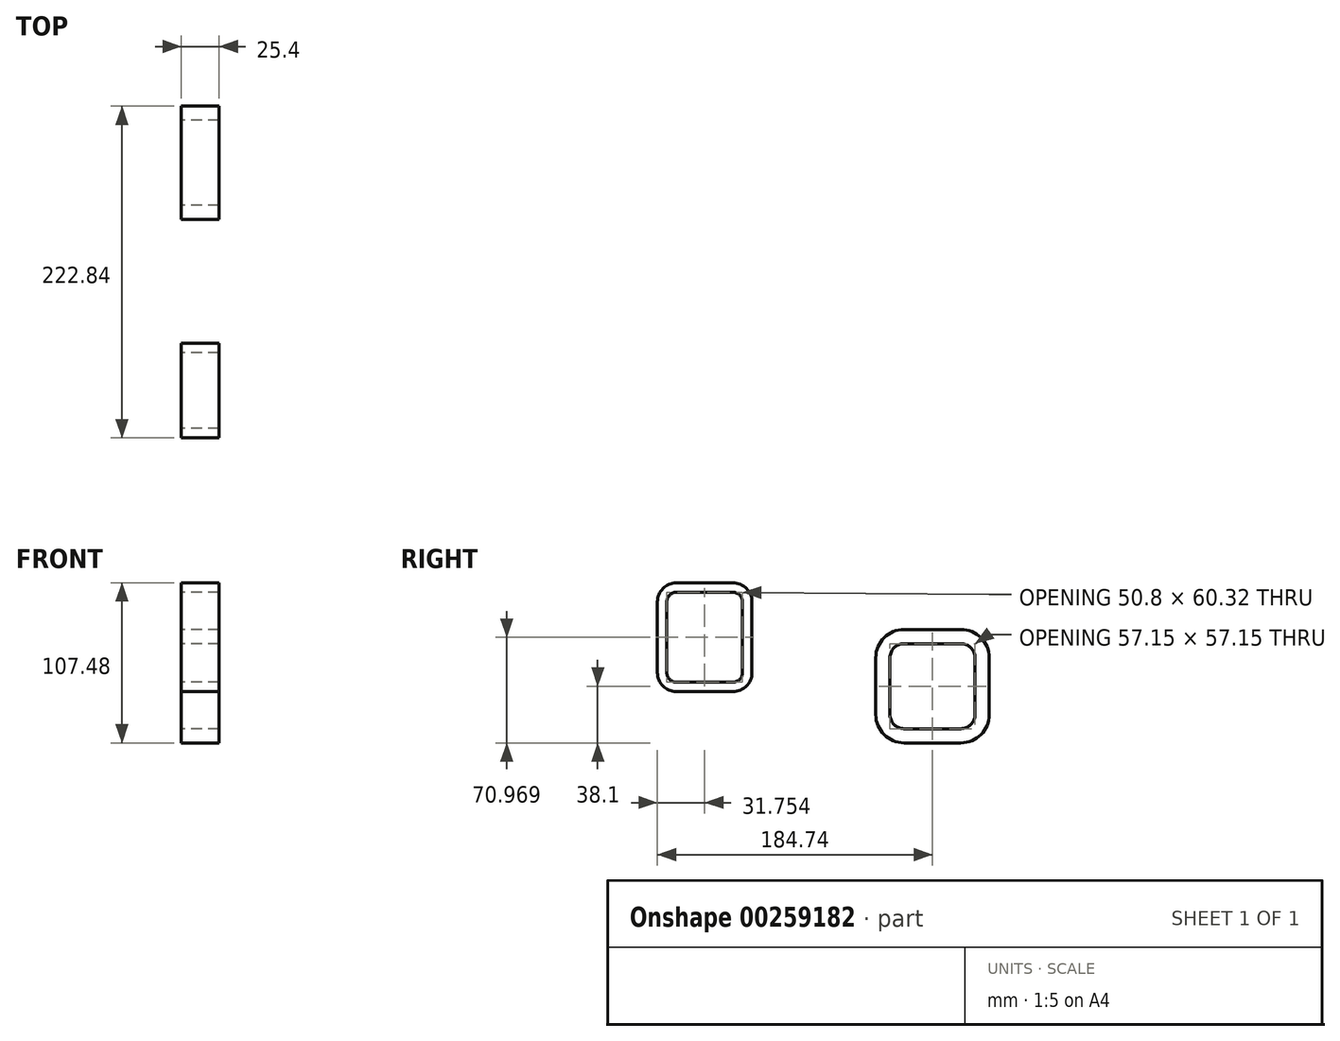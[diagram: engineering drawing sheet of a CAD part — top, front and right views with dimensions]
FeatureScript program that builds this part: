
annotation { "Feature Type Name" : "Feature", "Feature Type Description" : "" }
export const myFeature = defineFeature(function(context is Context, id is Id, definition is map)
    precondition{}
    {
        {
            var Q0;
            Q0=qCreatedBy(makeId("Right.planeOp"),FACE);
            var sketch = newSketch(context, id + "F0", { "sketchPlane" : qUnion([Q0])});
            skLineSegment(sketch, "E0.bottom", {"start": v(-19.05, 38.1) * mm, "end": v(19.05, 38.1) * mm});
            skLineSegment(sketch, "E0.top", {"start": v(-19.05, -38.1) * mm, "end": v(19.05, -38.1) * mm});
            skLineSegment(sketch, "E0.left", {"start": v(-38.1, 19.05) * mm, "end": v(-38.1, -19.05) * mm});
            skLineSegment(sketch, "E0.right", {"start": v(38.1, 19.05) * mm, "end": v(38.1, -19.05) * mm});
            skLineSegment(sketch, "E1.bottom", {"start": v(-19.05, 28.58) * mm, "end": v(19.05, 28.58) * mm});
            skLineSegment(sketch, "E1.top", {"start": v(-19.05, -28.58) * mm, "end": v(19.05, -28.58) * mm});
            skLineSegment(sketch, "E1.left", {"start": v(-28.58, 19.05) * mm, "end": v(-28.58, -19.05) * mm});
            skLineSegment(sketch, "E1.right", {"start": v(28.58, 19.05) * mm, "end": v(28.58, -19.05) * mm});
            skPoint(sketch, "E2.visualSharp", {"position": v(-28.58, 28.58) * mm});
            skArc(sketch, "E2.filletArc", {"start": v(-19.05, 28.58) * mm, "mid": v(-25.79, 25.79) * mm, "end": v(-28.58, 19.05) * mm});
            skPoint(sketch, "E3.visualSharp", {"position": v(-28.58, -28.58) * mm});
            skArc(sketch, "E3.filletArc", {"start": v(-28.58, -19.05) * mm, "mid": v(-25.79, -25.79) * mm, "end": v(-19.05, -28.58) * mm});
            skPoint(sketch, "E4.visualSharp", {"position": v(28.58, -28.58) * mm});
            skArc(sketch, "E4.filletArc", {"start": v(19.05, -28.58) * mm, "mid": v(25.79, -25.79) * mm, "end": v(28.58, -19.05) * mm});
            skPoint(sketch, "E5.visualSharp", {"position": v(28.58, 28.58) * mm});
            skArc(sketch, "E5.filletArc", {"start": v(28.58, 19.05) * mm, "mid": v(25.79, 25.79) * mm, "end": v(19.05, 28.58) * mm});
            skPoint(sketch, "E6.visualSharp", {"position": v(-38.1, 38.1) * mm});
            skArc(sketch, "E6.filletArc", {"start": v(-19.05, 38.1) * mm, "mid": v(-32.52, 32.52) * mm, "end": v(-38.1, 19.05) * mm});
            skPoint(sketch, "E7.visualSharp", {"position": v(-38.1, -38.1) * mm});
            skArc(sketch, "E7.filletArc", {"start": v(-38.1, -19.05) * mm, "mid": v(-32.52, -32.52) * mm, "end": v(-19.05, -38.1) * mm});
            skPoint(sketch, "E8.visualSharp", {"position": v(38.1, -38.1) * mm});
            skArc(sketch, "E8.filletArc", {"start": v(19.05, -38.1) * mm, "mid": v(32.52, -32.52) * mm, "end": v(38.1, -19.05) * mm});
            skPoint(sketch, "E9.visualSharp", {"position": v(38.1, 38.1) * mm});
            skArc(sketch, "E9.filletArc", {"start": v(38.1, 19.05) * mm, "mid": v(32.52, 32.52) * mm, "end": v(19.05, 38.1) * mm});
            skSolve(sketch);
        }
        {
            var Q0;
            Q0=qSketchRegion(id+"F0",true);
            extrude(context, id + "F1", {"entities" : qUnion([Q0]), "depth" : 25.4 * mm});
        }
        {
            var Q0;
            Q0=qCreatedBy(makeId("Right.planeOp"),FACE);
            var sketch = newSketch(context, id + "F2", { "sketchPlane" : qUnion([Q0])});
            skLineSegment(sketch, "E10.bottom", {"start": v(-172.04, 69.38) * mm, "end": v(-133.94, 69.38) * mm});
            skLineSegment(sketch, "E10.top", {"start": v(-172.04, -3.64) * mm, "end": v(-133.94, -3.64) * mm});
            skLineSegment(sketch, "E10.left", {"start": v(-184.74, 56.68) * mm, "end": v(-184.74, 9.06) * mm});
            skLineSegment(sketch, "E10.right", {"start": v(-121.24, 56.68) * mm, "end": v(-121.24, 9.06) * mm});
            skLineSegment(sketch, "E11.bottom", {"start": v(-172.04, 63.03) * mm, "end": v(-133.94, 63.03) * mm});
            skLineSegment(sketch, "E11.top", {"start": v(-172.04, 2.7) * mm, "end": v(-133.94, 2.7) * mm});
            skLineSegment(sketch, "E11.left", {"start": v(-178.39, 56.68) * mm, "end": v(-178.39, 9.06) * mm});
            skLineSegment(sketch, "E11.right", {"start": v(-127.59, 56.68) * mm, "end": v(-127.59, 9.06) * mm});
            skPoint(sketch, "E12.visualSharp", {"position": v(-178.39, 63.03) * mm});
            skArc(sketch, "E12.filletArc", {"start": v(-172.04, 63.03) * mm, "mid": v(-176.53, 61.17) * mm, "end": v(-178.39, 56.68) * mm});
            skPoint(sketch, "E13.visualSharp", {"position": v(-178.39, 2.7) * mm});
            skArc(sketch, "E13.filletArc", {"start": v(-178.39, 9.06) * mm, "mid": v(-176.53, 4.57) * mm, "end": v(-172.04, 2.7) * mm});
            skPoint(sketch, "E14.visualSharp", {"position": v(-127.59, 2.7) * mm});
            skArc(sketch, "E14.filletArc", {"start": v(-133.94, 2.7) * mm, "mid": v(-129.45, 4.57) * mm, "end": v(-127.59, 9.06) * mm});
            skPoint(sketch, "E15.visualSharp", {"position": v(-127.59, 63.03) * mm});
            skArc(sketch, "E15.filletArc", {"start": v(-127.59, 56.68) * mm, "mid": v(-129.45, 61.17) * mm, "end": v(-133.94, 63.03) * mm});
            skPoint(sketch, "E16.visualSharp", {"position": v(-184.74, 69.38) * mm});
            skArc(sketch, "E16.filletArc", {"start": v(-172.04, 69.38) * mm, "mid": v(-181.02, 65.66) * mm, "end": v(-184.74, 56.68) * mm});
            skPoint(sketch, "E17.visualSharp", {"position": v(-184.74, -3.64) * mm});
            skArc(sketch, "E17.filletArc", {"start": v(-184.74, 9.06) * mm, "mid": v(-181.02, 0.08) * mm, "end": v(-172.04, -3.64) * mm});
            skPoint(sketch, "E18.visualSharp", {"position": v(-121.24, -3.64) * mm});
            skArc(sketch, "E18.filletArc", {"start": v(-133.94, -3.64) * mm, "mid": v(-124.96, 0.08) * mm, "end": v(-121.24, 9.06) * mm});
            skPoint(sketch, "E19.visualSharp", {"position": v(-121.24, 69.38) * mm});
            skArc(sketch, "E19.filletArc", {"start": v(-121.24, 56.68) * mm, "mid": v(-124.96, 65.66) * mm, "end": v(-133.94, 69.38) * mm});
            skSolve(sketch);
        }
        {
            var Q0;
            Q0 = qSketchRegion(id + "F2", true);
            extrude(context, id + "F3", {"entities" : qUnion([Q0]), "depth" : 25.4 * mm});
        }
    });
